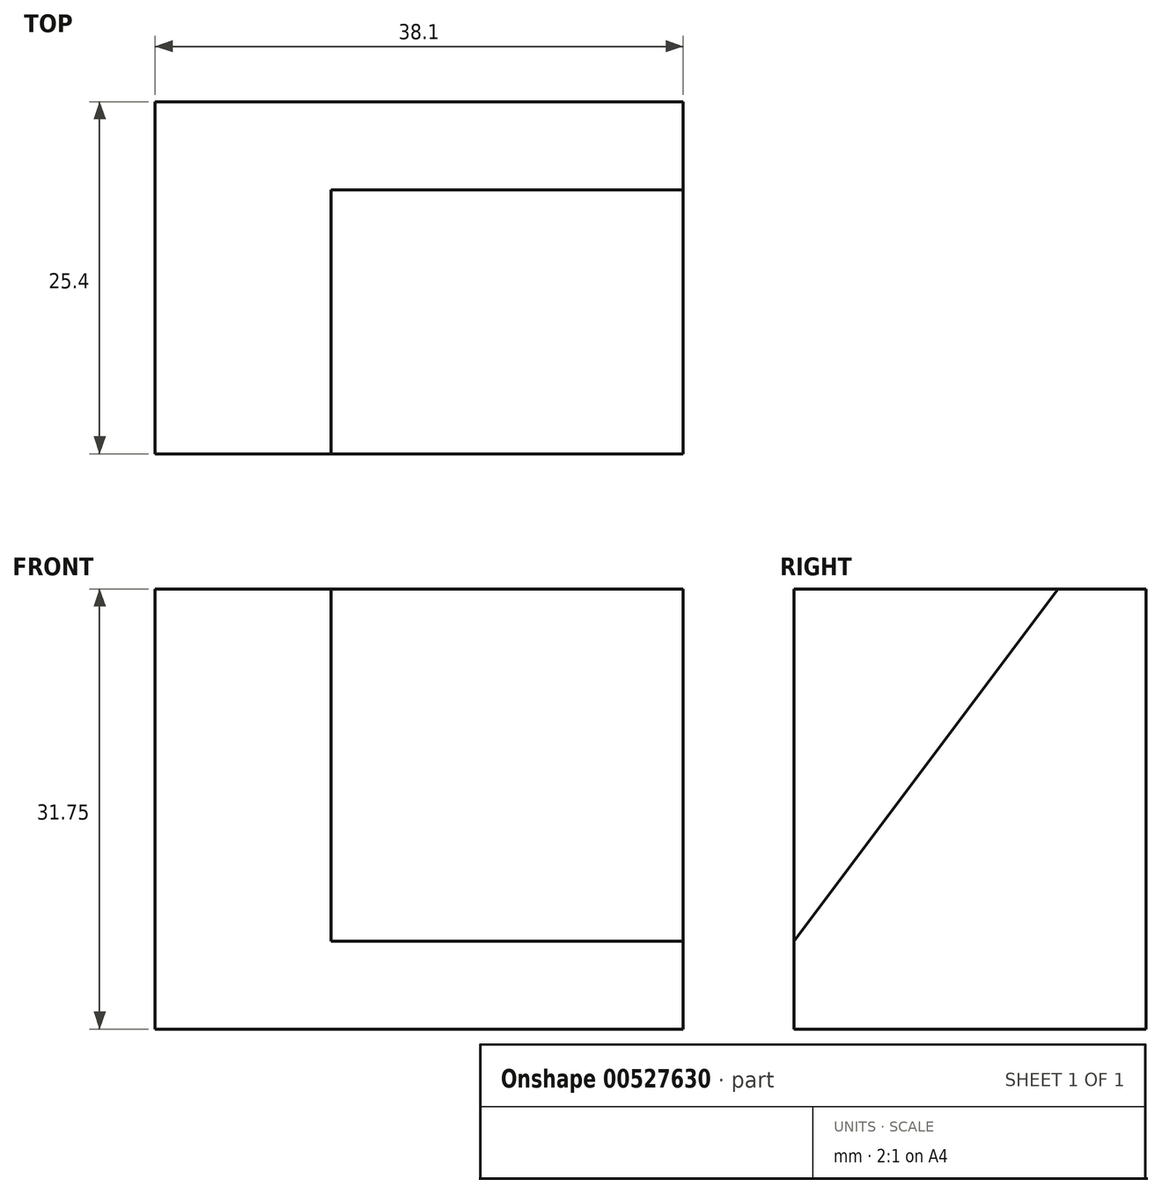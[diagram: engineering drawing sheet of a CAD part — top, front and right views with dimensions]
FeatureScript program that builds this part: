
annotation { "Feature Type Name" : "Feature", "Feature Type Description" : "" }
export const myFeature = defineFeature(function(context is Context, id is Id, definition is map)
    precondition{}
    {
        {
            var Q0;
            Q0=qCreatedBy(makeId("Front.planeOp"),FACE);
            var sketch = newSketch(context, id + "F0", { "sketchPlane" : qUnion([Q0])});
            skLineSegment(sketch, "E0", {"start": v(0, 0) * mm, "end": v(38.1, 0) * mm});
            skLineSegment(sketch, "E1", {"start": v(38.1, 0) * mm, "end": v(38.1, 31.75) * mm});
            skLineSegment(sketch, "E2", {"start": v(38.1, 31.75) * mm, "end": v(0, 31.75) * mm});
            skLineSegment(sketch, "E3", {"start": v(0, 31.75) * mm, "end": v(0, 0) * mm});
            skSolve(sketch);
        }
        {
            var Q0;
            Q0 = qSketchRegion(id + "F0", true);
            extrude(context, id + "F1", {"entities" : qUnion([Q0]), "depth" : 25.4 * mm, "offsetDistance" : 25.4 * mm});
        }
        {
            var Q0;
            Q0=makeQuery(id+"F1.opExtrude","SWEPT_FACE",FACE,{"disambiguationData":[OSD([sQuery(id+"F0.wireOp",EDGE,"E1")])]});
            var sketch = newSketch(context, id + "F2", { "sketchPlane" : qUnion([Q0])});
            skLineSegment(sketch, "E4", {"start": v(-6.35, 31.75) * mm, "end": v(-25.4, 6.35) * mm});
            skSolve(sketch);
        }
        {
            var Q0;
            Q0 = qSketchRegion(id + "F2", true);
            var Q1;
            {var subQ0=sQuery(id+"F2.wireOp",EDGE,"E4");var subQ1=sQuery(id+"F0.wireOp",EDGE,"E1");var subQ4=makeQuery(id+"F1.opExtrude","CAP_EDGE",EDGE,{"disambiguationData":[OSD([subQ1])],"isStart":false});var subQ5=makeQuery(id+"F2.imprint","INTERSECT",VERTEX,{"disambiguationData":[OD(1.0)],"derivedFrom":[subQ4,subQ0]});Q1=makeQuery(id+"F2.imprint","IMPRINT",FACE,{"disambiguationData":[TD([[makeQuery(id+"F2.imprint","IMPRINT",EDGE,{"disambiguationData":[TD([[subQ5,1.0]])],"derivedFrom":subQ0}),-1.0]])]});}
            extrude(context, id + "F3", {"entities" : qUnion([Q0, Q1]), "operationType" : NewBodyOperationType.REMOVE, "oppositeDirection" : true, "depth" : 25.4 * mm, "offsetDistance" : 25.4 * mm});
        }
        {
            var Q0;
            {var subQ0=sQuery(id+"F2.wireOp",EDGE,"E4");var subQ1=sQuery(id+"F0.wireOp",EDGE,"E1");var subQ4=makeQuery(id+"F1.opExtrude","CAP_EDGE",EDGE,{"disambiguationData":[OSD([subQ1])],"isStart":false});var subQ5=makeQuery(id+"F2.imprint","INTERSECT",VERTEX,{"disambiguationData":[OD(1.0)],"derivedFrom":[subQ4,subQ0]});Q0=makeQuery(id+"F2.imprint","IMPRINT",FACE,{"disambiguationData":[TD([[makeQuery(id+"F2.imprint","IMPRINT",EDGE,{"disambiguationData":[TD([[subQ5,1.0]])],"derivedFrom":subQ0}),-1.0]])]});}
            extrude(context, id + "F4", {"entities" : qUnion([Q0]), "operationType" : NewBodyOperationType.REMOVE, "oppositeDirection" : true, "depth" : 25.4 * mm, "offsetDistance" : 25.4 * mm});
        }
    });
